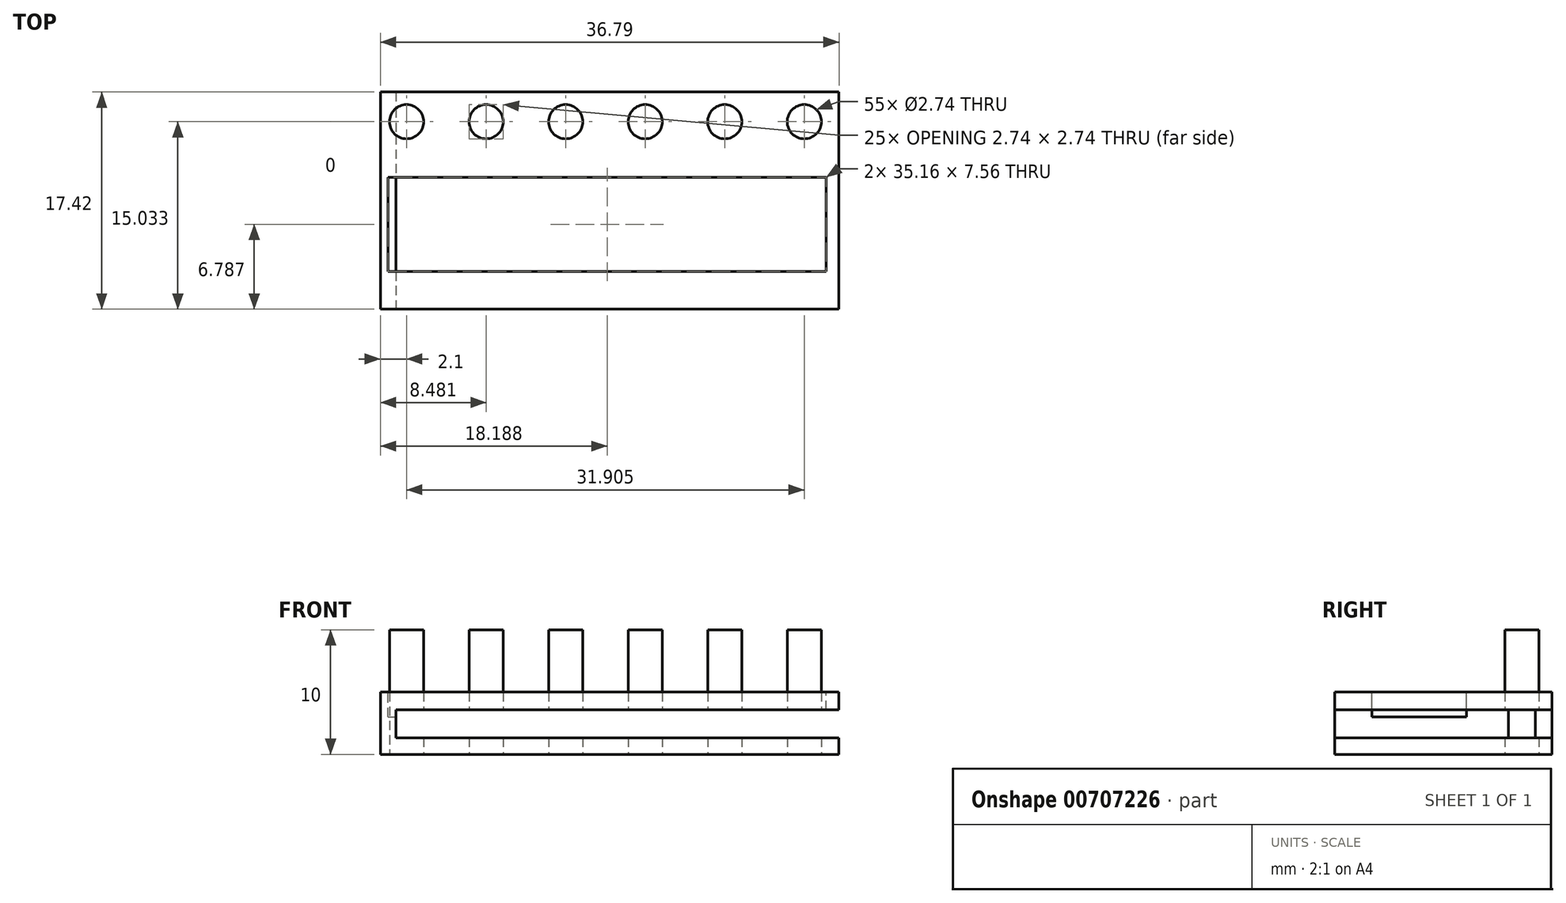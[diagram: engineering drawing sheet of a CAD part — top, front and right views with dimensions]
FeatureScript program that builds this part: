
annotation { "Feature Type Name" : "Feature", "Feature Type Description" : "" }
export const myFeature = defineFeature(function(context is Context, id is Id, definition is map)
    precondition{}
    {
        {
            var Q0;
            Q0=qCreatedBy(makeId("Top.planeOp"),FACE);
            var sketch = newSketch(context, id + "F0", { "sketchPlane" : qUnion([Q0])});
            skLineSegment(sketch, "E0.bottom", {"start": v(0, 0) * mm, "end": v(36.79, 0) * mm});
            skLineSegment(sketch, "E0.top", {"start": v(0, 17.42) * mm, "end": v(36.79, 17.42) * mm});
            skLineSegment(sketch, "E0.left", {"start": v(0, 0) * mm, "end": v(0, 17.42) * mm});
            skLineSegment(sketch, "E0.right", {"start": v(36.79, 0) * mm, "end": v(36.79, 17.42) * mm});
            skCircle(sketch, "E1", {"center": v(2.1, 15.03) * mm, "radius": 1.37 * mm});
            skCircle(sketch, "E2.1.0.0", {"center": v(8.48, 15.03) * mm, "radius": 1.37 * mm});
            skCircle(sketch, "E2.2.0.0", {"center": v(14.86, 15.03) * mm, "radius": 1.37 * mm});
            skCircle(sketch, "E2.3.0.0", {"center": v(21.24, 15.03) * mm, "radius": 1.37 * mm});
            skCircle(sketch, "E2.4.0.0", {"center": v(27.62, 15.03) * mm, "radius": 1.37 * mm});
            skCircle(sketch, "E2.5.0.0", {"center": v(34, 15.03) * mm, "radius": 1.37 * mm});
            skLineSegment(sketch, "E2.direction1", {"start": v(2.1, 15.03) * mm, "end": v(8.48, 15.03) * mm, "construction": true});
            skSolve(sketch);
        }
        {
            var Q0;
            Q0=makeQuery(id+"F0.imprint","IMPRINT",FACE,{"disambiguationData":[TD([[makeQuery(id+"F0.imprint","IMPRINT",EDGE,{"derivedFrom":sQuery(id+"F0.wireOp",EDGE,"E2.1.0.0")}),1.0]])]});
            var Q1;
            Q1=makeQuery(id+"F0.imprint","IMPRINT",FACE,{"disambiguationData":[TD([[makeQuery(id+"F0.imprint","IMPRINT",EDGE,{"derivedFrom":sQuery(id+"F0.wireOp",EDGE,"E2.2.0.0")}),1.0]])]});
            var Q2;
            Q2=makeQuery(id+"F0.imprint","IMPRINT",FACE,{"disambiguationData":[TD([[makeQuery(id+"F0.imprint","IMPRINT",EDGE,{"derivedFrom":sQuery(id+"F0.wireOp",EDGE,"E2.3.0.0")}),1.0]])]});
            var Q3;
            Q3=makeQuery(id+"F0.imprint","IMPRINT",FACE,{"disambiguationData":[TD([[makeQuery(id+"F0.imprint","IMPRINT",EDGE,{"derivedFrom":sQuery(id+"F0.wireOp",EDGE,"E2.4.0.0")}),1.0]])]});
            var Q4;
            Q4=makeQuery(id+"F0.imprint","IMPRINT",FACE,{"disambiguationData":[TD([[makeQuery(id+"F0.imprint","IMPRINT",EDGE,{"derivedFrom":sQuery(id+"F0.wireOp",EDGE,"E2.5.0.0")}),1.0]])]});
            var Q5;
            Q5=makeQuery(id+"F0.imprint","IMPRINT",FACE,{"disambiguationData":[TD([[makeQuery(id+"F0.imprint","IMPRINT",EDGE,{"derivedFrom":sQuery(id+"F0.wireOp",EDGE,"E1")}),1.0]])]});
            extrude(context, id + "F1", {"entities" : qUnion([Q0, Q1, Q2, Q3, Q4, Q5]), "depth" : 10 * mm, "offsetDistance" : 25 * mm});
        }
        {
            var Q0;
            Q0=makeQuery(id+"F0.imprint","IMPRINT",FACE,{"disambiguationData":[TD([[makeQuery(id+"F0.imprint","IMPRINT",EDGE,{"derivedFrom":sQuery(id+"F0.wireOp",EDGE,"E0.bottom")}),1.0]])]});
            extrude(context, id + "F2", {"entities" : qUnion([Q0]), "depth" : 5 * mm, "offsetDistance" : 25 * mm});
        }
        {
            var Q0;
            Q0=makeQuery(id+"F2.opExtrude","CAP_FACE",FACE,{"disambiguationData":[OSD([sQuery(id+"F0.wireOp",EDGE,"E0.bottom"),sQuery(id+"F0.wireOp",EDGE,"E0.top"),sQuery(id+"F0.wireOp",EDGE,"E0.left"),sQuery(id+"F0.wireOp",EDGE,"E0.right"),sQuery(id+"F0.wireOp",EDGE,"E1"),sQuery(id+"F0.wireOp",EDGE,"E2.1.0.0"),sQuery(id+"F0.wireOp",EDGE,"E2.2.0.0"),sQuery(id+"F0.wireOp",EDGE,"E2.3.0.0"),sQuery(id+"F0.wireOp",EDGE,"E2.4.0.0"),sQuery(id+"F0.wireOp",EDGE,"E2.5.0.0")])],"isStart":false});
            var sketch = newSketch(context, id + "F3", { "sketchPlane" : qUnion([Q0])});
            skLineSegment(sketch, "E3.bottom", {"start": v(0.6, 10.57) * mm, "end": v(35.77, 10.57) * mm});
            skLineSegment(sketch, "E3.top", {"start": v(0.6, 3) * mm, "end": v(35.77, 3) * mm});
            skLineSegment(sketch, "E3.left", {"start": v(0.6, 10.57) * mm, "end": v(0.6, 3) * mm});
            skLineSegment(sketch, "E3.right", {"start": v(35.77, 10.57) * mm, "end": v(35.77, 3) * mm});
            skSolve(sketch);
        }
        {
            var Q0;
            Q0=makeQuery(id+"F3.imprint","IMPRINT",FACE,{"disambiguationData":[TD([[makeQuery(id+"F3.imprint","IMPRINT",EDGE,{"derivedFrom":sQuery(id+"F3.wireOp",EDGE,"E3.bottom")}),-1.0]])]});
            var Q1;
            Q1=sQuery(id+"F3.wireOp",EDGE,"E3.left");
            extrude(context, id + "F4", {"entities" : qUnion([Q0]), "operationType" : NewBodyOperationType.REMOVE, "surfaceEntities" : qUnion([Q1]), "oppositeDirection" : true, "depth" : 2 * mm, "offsetDistance" : 25 * mm});
        }
        {
            var Q0;
            Q0=makeQuery(id+"F2.opExtrude","SWEPT_FACE",FACE,{"disambiguationData":[OSD([sQuery(id+"F0.wireOp",EDGE,"E0.bottom")])]});
            var sketch = newSketch(context, id + "F5", { "sketchPlane" : qUnion([Q0])});
            skLineSegment(sketch, "E4.bottom", {"start": v(1.25, 5) * mm, "end": v(36.79, 5) * mm});
            skLineSegment(sketch, "E4.top", {"start": v(1.25, 1.34) * mm, "end": v(36.79, 1.34) * mm});
            skLineSegment(sketch, "E4.left", {"start": v(1.25, 3.57) * mm, "end": v(1.25, 1.34) * mm});
            skLineSegment(sketch, "E5.bottom", {"start": v(1.25, 1.34) * mm, "end": v(37.6, 1.34) * mm});
            skLineSegment(sketch, "E5.top", {"start": v(1.25, 3.57) * mm, "end": v(37.6, 3.57) * mm});
            skLineSegment(sketch, "E5.left", {"start": v(1.25, 1.34) * mm, "end": v(1.25, 3.57) * mm});
            skLineSegment(sketch, "E5.right", {"start": v(37.6, 1.34) * mm, "end": v(37.6, 3.57) * mm});
            skSolve(sketch);
        }
        {
            var Q0;
            Q0 = qSketchRegion(id + "F5", true);
            extrude(context, id + "F6", {"entities" : qUnion([Q0]), "operationType" : NewBodyOperationType.REMOVE, "oppositeDirection" : true, "depth" : 25 * mm, "offsetDistance" : 25 * mm});
        }
    });
